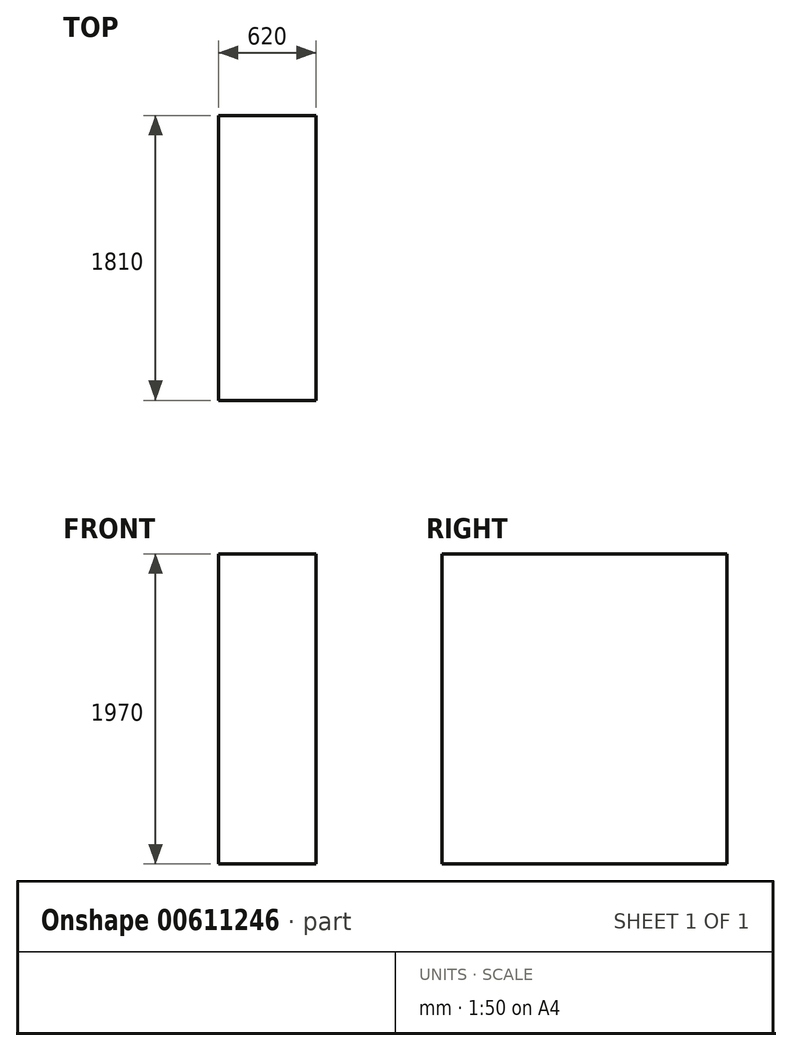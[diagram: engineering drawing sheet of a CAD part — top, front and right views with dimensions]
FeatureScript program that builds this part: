
annotation { "Feature Type Name" : "Feature", "Feature Type Description" : "" }
export const myFeature = defineFeature(function(context is Context, id is Id, definition is map)
    precondition{}
    {
        {
            var Q0;
            Q0=qCreatedBy(makeId("Top.planeOp"),FACE);
            var sketch = newSketch(context, id + "F0", { "sketchPlane" : qUnion([Q0])});
            skLineSegment(sketch, "E0.bottom", {"start": v(-620, 1810) * mm, "end": v(0, 1810) * mm});
            skLineSegment(sketch, "E0.top", {"start": v(-620, 0) * mm, "end": v(0, 0) * mm});
            skLineSegment(sketch, "E0.left", {"start": v(-620, 1810) * mm, "end": v(-620, 0) * mm});
            skLineSegment(sketch, "E0.right", {"start": v(0, 1810) * mm, "end": v(0, 0) * mm});
            skSolve(sketch);
        }
        {
            var Q0;
            Q0=makeQuery(id+"F0.imprint","IMPRINT",FACE,{"disambiguationData":[TD([[makeQuery(id+"F0.imprint","IMPRINT",EDGE,{"derivedFrom":sQuery(id+"F0.wireOp",EDGE,"E0.bottom")}),-1.0]])]});
            extrude(context, id + "F1", {"entities" : qUnion([Q0]), "depth" : 1970 * mm, "offsetDistance" : 25 * mm});
        }
    });
